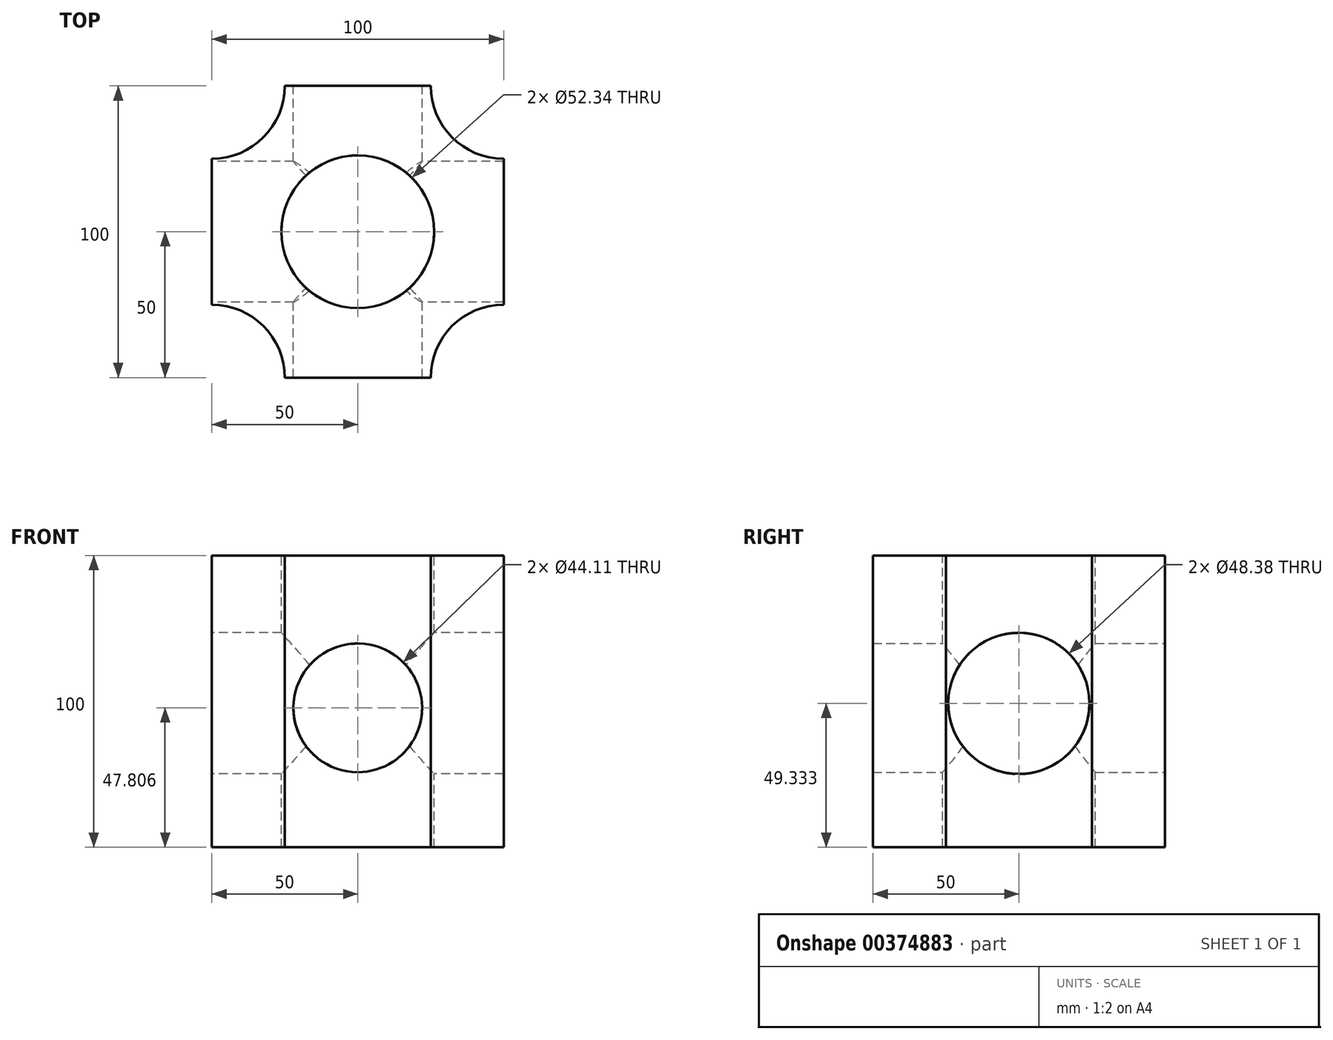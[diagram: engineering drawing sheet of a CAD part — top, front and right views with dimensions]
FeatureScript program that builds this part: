
annotation { "Feature Type Name" : "Feature", "Feature Type Description" : "" }
export const myFeature = defineFeature(function(context is Context, id is Id, definition is map)
    precondition{}
    {
        {
            var Q0;
            Q0=qCreatedBy(makeId("Top.planeOp"),FACE);
            var sketch = newSketch(context, id + "F0", { "sketchPlane" : qUnion([Q0])});
            skLineSegment(sketch, "E0.bottom", {"start": v(50, 50) * mm, "end": v(-50, 50) * mm});
            skLineSegment(sketch, "E0.top", {"start": v(50, -50) * mm, "end": v(-50, -50) * mm});
            skLineSegment(sketch, "E0.left", {"start": v(50, 50) * mm, "end": v(50, -50) * mm});
            skLineSegment(sketch, "E0.right", {"start": v(-50, 50) * mm, "end": v(-50, -50) * mm});
            skPoint(sketch, "E0.middle", {"position": v(0, 0) * mm});
            skSolve(sketch);
        }
        {
            var Q0;
            Q0=makeQuery(id+"F0.imprint","IMPRINT",FACE,{"disambiguationData":[TD([[makeQuery(id+"F0.imprint","IMPRINT",EDGE,{"derivedFrom":sQuery(id+"F0.wireOp",EDGE,"E0.bottom")}),1.0]])]});
            extrude(context, id + "F1", {"entities" : qUnion([Q0]), "depth" : 100 * mm});
        }
        {
            var Q0;
            Q0=makeQuery(id+"F1.opExtrude","CAP_FACE",FACE,{"disambiguationData":[OSD([sQuery(id+"F0.wireOp",EDGE,"E0.bottom"),sQuery(id+"F0.wireOp",EDGE,"E0.top"),sQuery(id+"F0.wireOp",EDGE,"E0.left"),sQuery(id+"F0.wireOp",EDGE,"E0.right")])],"isStart":false});
            var sketch = newSketch(context, id + "F2", { "sketchPlane" : qUnion([Q0])});
            skCircle(sketch, "E1", {"center": v(0, 0) * mm, "radius": 26.17 * mm});
            skSolve(sketch);
        }
        {
            var Q0;
            Q0=makeQuery(id+"F2.imprint","IMPRINT",FACE,{"disambiguationData":[TD([[makeQuery(id+"F2.imprint","IMPRINT",EDGE,{"derivedFrom":sQuery(id+"F2.wireOp",EDGE,"E1")}),1.0]])]});
            extrude(context, id + "F3", {"entities" : qUnion([Q0]), "operationType" : NewBodyOperationType.REMOVE, "oppositeDirection" : true, "depth" : 100 * mm});
        }
        {
            var Q0;
            Q0=makeQuery(id+"F1.opExtrude","CAP_FACE",FACE,{"disambiguationData":[OSD([sQuery(id+"F0.wireOp",EDGE,"E0.bottom"),sQuery(id+"F0.wireOp",EDGE,"E0.top"),sQuery(id+"F0.wireOp",EDGE,"E0.left"),sQuery(id+"F0.wireOp",EDGE,"E0.right")])],"isStart":false});
            var sketch = newSketch(context, id + "F4", { "sketchPlane" : qUnion([Q0])});
            skLineSegment(sketch, "E2.bottom", {"start": v(-50, 50) * mm, "end": v(-25, 50) * mm});
            skLineSegment(sketch, "E2.top", {"start": v(-50, 25) * mm, "end": v(-25, 25) * mm});
            skLineSegment(sketch, "E2.left", {"start": v(-50, 50) * mm, "end": v(-50, 25) * mm});
            skLineSegment(sketch, "E2.right", {"start": v(-25, 50) * mm, "end": v(-25, 25) * mm});
            skLineSegment(sketch, "E3.bottom", {"start": v(50, 50) * mm, "end": v(25, 50) * mm});
            skLineSegment(sketch, "E3.top", {"start": v(50, 25) * mm, "end": v(25, 25) * mm});
            skLineSegment(sketch, "E3.left", {"start": v(50, 50) * mm, "end": v(50, 25) * mm});
            skLineSegment(sketch, "E3.right", {"start": v(25, 50) * mm, "end": v(25, 25) * mm});
            skLineSegment(sketch, "E4.bottom", {"start": v(-50, -50) * mm, "end": v(-25, -50) * mm});
            skLineSegment(sketch, "E4.top", {"start": v(-50, -25) * mm, "end": v(-25, -25) * mm});
            skLineSegment(sketch, "E4.left", {"start": v(-50, -50) * mm, "end": v(-50, -25) * mm});
            skLineSegment(sketch, "E4.right", {"start": v(-25, -50) * mm, "end": v(-25, -25) * mm});
            skLineSegment(sketch, "E5.bottom", {"start": v(50, -50) * mm, "end": v(25, -50) * mm});
            skLineSegment(sketch, "E5.top", {"start": v(50, -25) * mm, "end": v(25, -25) * mm});
            skLineSegment(sketch, "E5.left", {"start": v(50, -50) * mm, "end": v(50, -25) * mm});
            skLineSegment(sketch, "E5.right", {"start": v(25, -50) * mm, "end": v(25, -25) * mm});
            skSolve(sketch);
        }
        {
            var Q0;
            Q0=makeQuery(id+"F4.imprint","IMPRINT",FACE,{"disambiguationData":[TD([[makeQuery(id+"F4.imprint","IMPRINT",EDGE,{"derivedFrom":sQuery(id+"F4.wireOp",EDGE,"E3.bottom")}),1.0]])]});
            var Q1;
            Q1 = qSketchRegion(id + "F4", true);
            extrude(context, id + "F5", {"entities" : qUnion([Q0, Q1]), "operationType" : NewBodyOperationType.REMOVE, "oppositeDirection" : true, "depth" : 125.4 * mm});
        }
        {
            var Q0;
            Q0=makeQuery(id+"F5.boolean.opBoolean","COPY",EDGE,{"derivedFrom":makeQuery(id+"F5.opExtrude","SWEPT_EDGE",EDGE,{"disambiguationData":[OSD([sQuery(id+"F4.wireOp",EDGE,"E4.top"),sQuery(id+"F4.wireOp",EDGE,"E4.right")])]})});
            var Q1;
            Q1=makeQuery(id+"F5.boolean.opBoolean","COPY",EDGE,{"derivedFrom":makeQuery(id+"F5.opExtrude","SWEPT_EDGE",EDGE,{"disambiguationData":[OSD([sQuery(id+"F4.wireOp",EDGE,"E5.top"),sQuery(id+"F4.wireOp",EDGE,"E5.right")])]})});
            var Q2;
            Q2=makeQuery(id+"F5.boolean.opBoolean","COPY",EDGE,{"derivedFrom":makeQuery(id+"F5.opExtrude","SWEPT_EDGE",EDGE,{"disambiguationData":[OSD([sQuery(id+"F4.wireOp",EDGE,"E3.top"),sQuery(id+"F4.wireOp",EDGE,"E3.right")])]})});
            var Q3;
            Q3=makeQuery(id+"F5.boolean.opBoolean","COPY",EDGE,{"derivedFrom":makeQuery(id+"F5.opExtrude","SWEPT_EDGE",EDGE,{"disambiguationData":[OSD([sQuery(id+"F4.wireOp",EDGE,"E2.top"),sQuery(id+"F4.wireOp",EDGE,"E2.right")])]})});
            fillet(context, id + "F6", {"entities" : qUnion([Q0, Q1, Q2, Q3]), "radius" : 25 * mm, "tangentPropagation" : true, "allowEdgeOverflow" : false});
        }
        {
            var Q0;
            Q0=makeQuery(id+"F1.opExtrude","SWEPT_FACE",FACE,{"disambiguationData":[OSD([sQuery(id+"F0.wireOp",EDGE,"E0.right")])]});
            var sketch = newSketch(context, id + "F7", { "sketchPlane" : qUnion([Q0])});
            skCircle(sketch, "E6", {"center": v(0, 49.33) * mm, "radius": 24.19 * mm});
            skSolve(sketch);
        }
        {
            var Q0;
            Q0=makeQuery(id+"F7.imprint","IMPRINT",FACE,{"disambiguationData":[TD([[makeQuery(id+"F7.imprint","IMPRINT",EDGE,{"derivedFrom":sQuery(id+"F7.wireOp",EDGE,"E6")}),1.0]])]});
            extrude(context, id + "F8", {"entities" : qUnion([Q0]), "operationType" : NewBodyOperationType.REMOVE, "oppositeDirection" : true, "depth" : 116.34 * mm});
        }
        {
            var Q0;
            Q0=makeQuery(id+"F1.opExtrude","SWEPT_FACE",FACE,{"disambiguationData":[OSD([sQuery(id+"F0.wireOp",EDGE,"E0.bottom")])]});
            var sketch = newSketch(context, id + "F9", { "sketchPlane" : qUnion([Q0])});
            skCircle(sketch, "E7", {"center": v(0, 47.8) * mm, "radius": 22.05 * mm});
            skSolve(sketch);
        }
        {
            var Q0;
            Q0=makeQuery(id+"F9.imprint","IMPRINT",FACE,{"disambiguationData":[TD([[makeQuery(id+"F9.imprint","IMPRINT",EDGE,{"derivedFrom":sQuery(id+"F9.wireOp",EDGE,"E7")}),1.0]])]});
            extrude(context, id + "F10", {"entities" : qUnion([Q0]), "operationType" : NewBodyOperationType.REMOVE, "oppositeDirection" : true, "depth" : 146.75 * mm});
        }
    });
